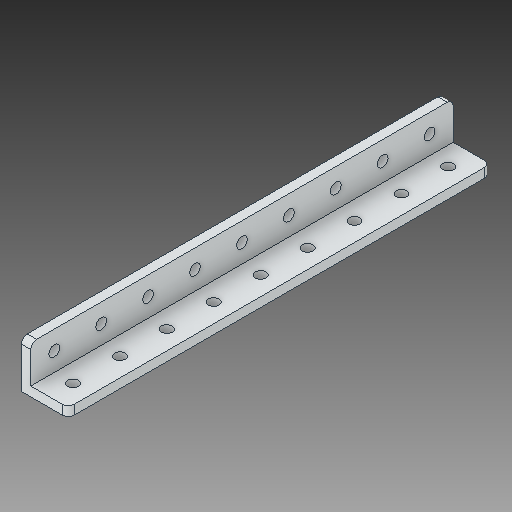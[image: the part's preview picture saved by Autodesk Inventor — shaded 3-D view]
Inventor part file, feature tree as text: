
AUTODESK INVENTOR PART (.ipt)
format: ipt  version: 2018 (Build 220112000, 112)  size: 151,552 bytes
history: native  units: in
note: dims shown in document units (in); Inventor stores cm internally (conversion verified against a paired STEP export)
features: fillet x1
ambient origin geometry x8: Origin, YZ Plane, XZ Plane, XY Plane, X Axis, Y Axis, Z Axis, Center Point
bodies: Solid1 (feature_tree)
feature tree (1):
  fillet  "Fillet1"  [1 undecoded]
note: 1 required parameter value undecoded (feature->parameter linkage not recoverable at this tier; creation-order binding heuristic only, values carry confidence <= 0.55)
